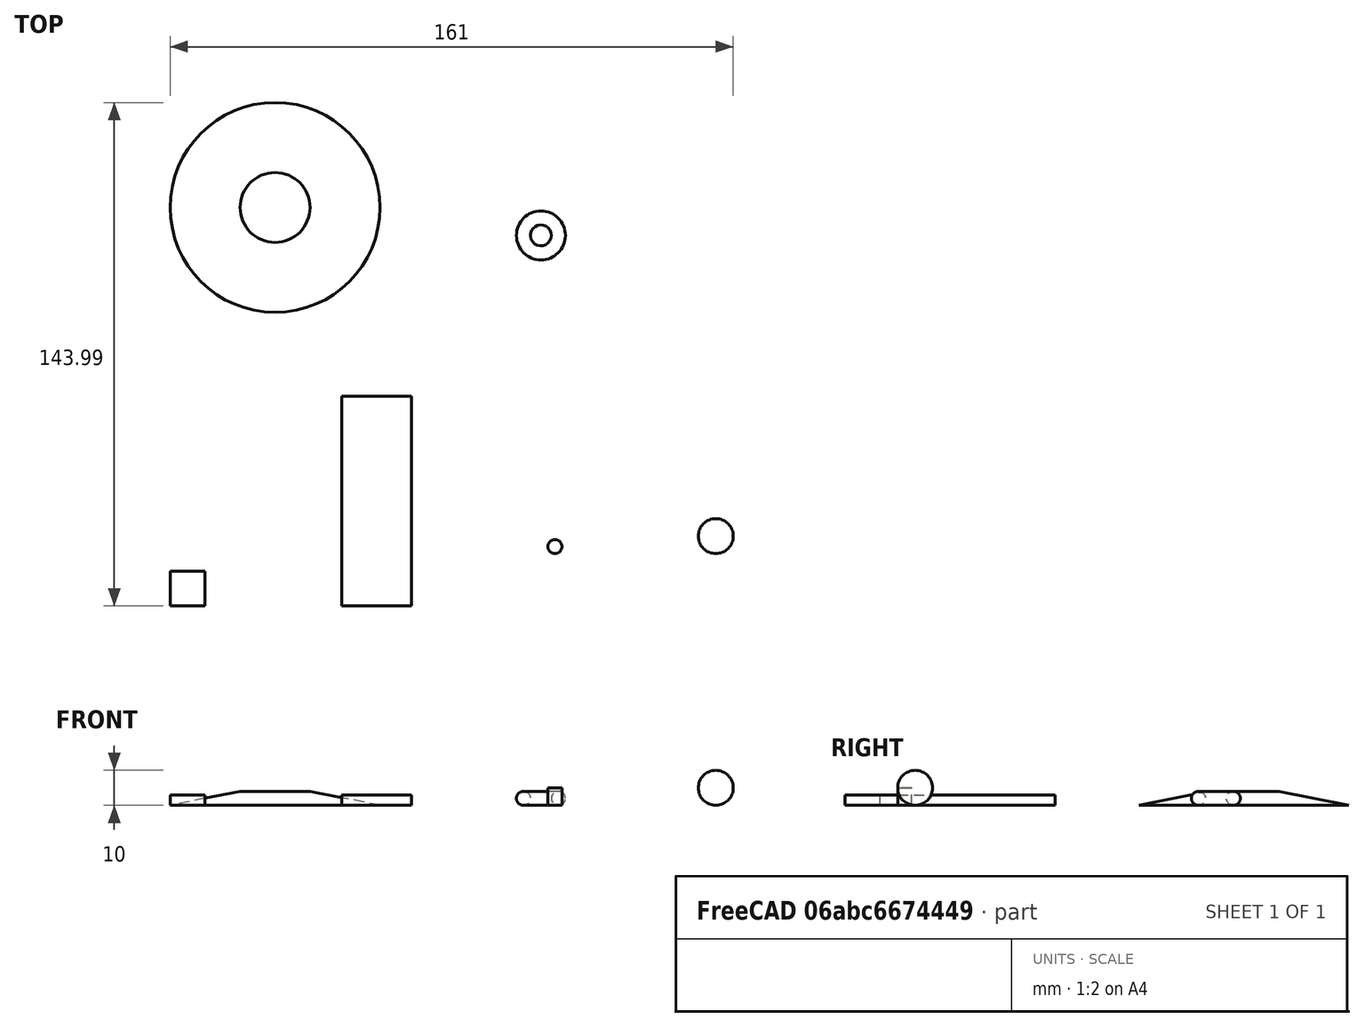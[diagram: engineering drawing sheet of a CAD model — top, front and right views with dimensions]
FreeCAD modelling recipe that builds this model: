
FCSTD DOCUMENT  (FreeCAD 0.16R6703 (Git))
Label: shapes-test2-result
License: All rights reserved
LicenseURL: http://en.wikipedia.org/wiki/All_rights_reserved
objects: Part::Box×2, Part::Cylinder×1, Part::Sphere×1, Part::Cone×1, Part::Torus×1
note: 6 computed .brp shape members not serialized (recipe doc carries the construction recipe); baked Part::Feature solids carry a one-line shape summary decoded from their .brp

FEATURE [Part::Box] Box  label="Cube"
  Height = 3
  Length = 10
  Width = 10
FEATURE [Part::Box] Box001  label="Cube001"
  Height = 3
  Length = 20
  Placement = pos=(49,0,0) rot=(0,0,1;0rad)
  Width = 60
FEATURE [Part::Cylinder] Cylinder
  Angle = 360
  Height = 5
  Placement = pos=(110,17,0) rot=(0,0,1;0rad)
  Radius = 2
FEATURE [Part::Sphere] Sphere
  Angle1 = -90
  Angle2 = 90
  Angle3 = 360
  Placement = pos=(156,19.9978,5) rot=(0,0,1;0rad)
  Radius = 5
FEATURE [Part::Cone] Cone
  Angle = 360
  Height = 4
  Placement = pos=(30,113.989,0) rot=(0,0,1;0rad)
  Radius1 = 30
  Radius2 = 10
FEATURE [Part::Torus] Torus
  Angle1 = -180
  Angle2 = 180
  Angle3 = 360
  Placement = pos=(106,105.977,1.99707) rot=(0,0,1;0rad)
  Radius1 = 5
  Radius2 = 2
